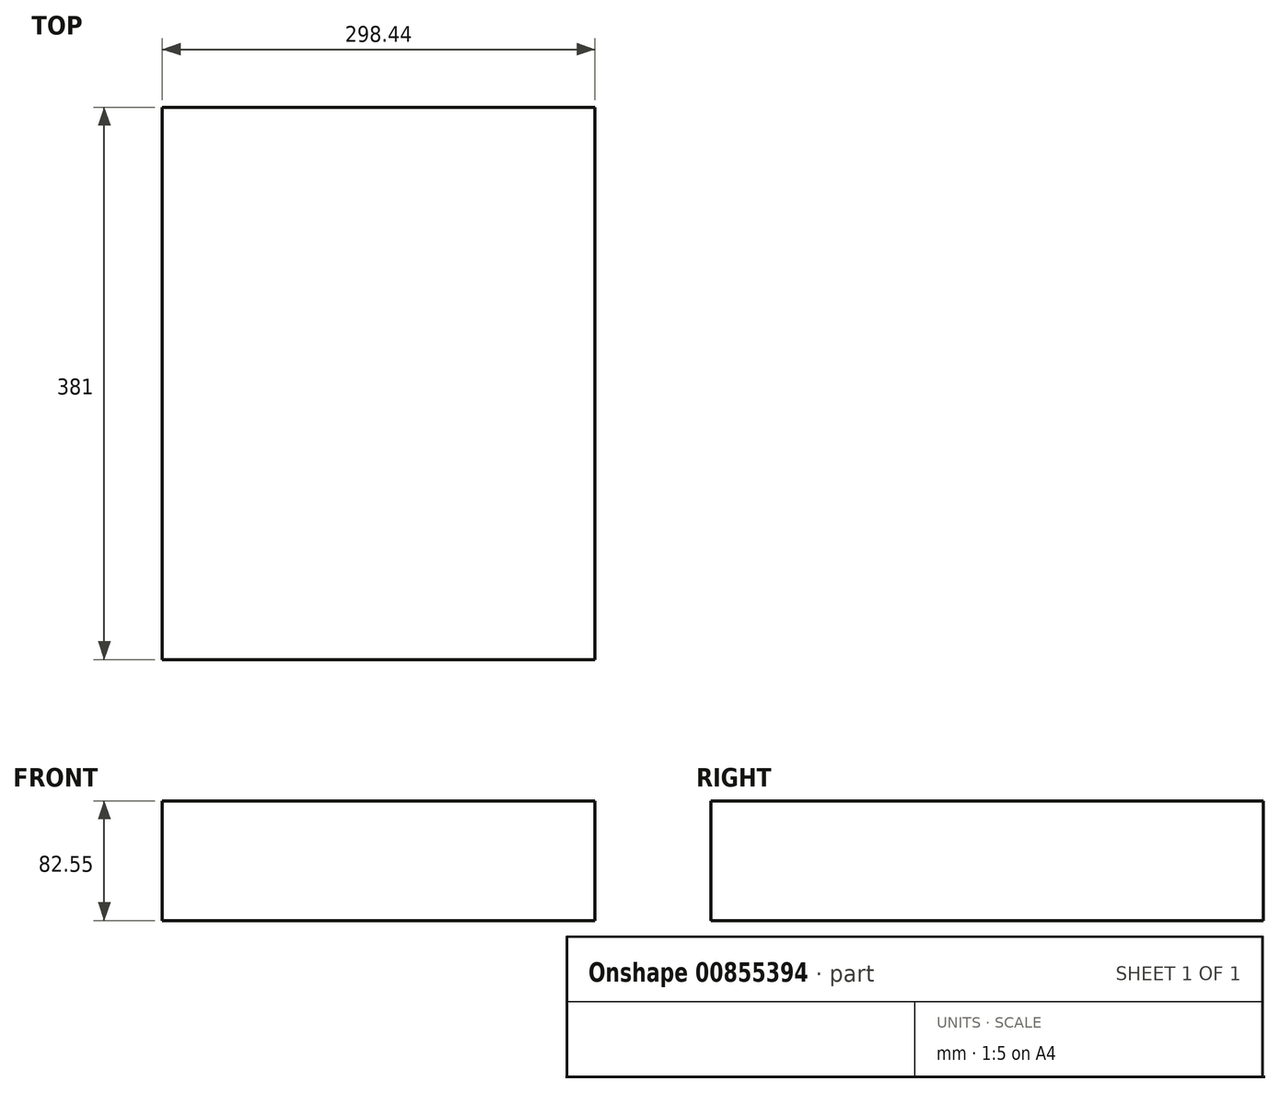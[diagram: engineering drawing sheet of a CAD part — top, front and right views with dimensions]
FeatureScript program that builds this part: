
annotation { "Feature Type Name" : "Feature", "Feature Type Description" : "" }
export const myFeature = defineFeature(function(context is Context, id is Id, definition is map)
    precondition{}
    {
        {
            var Q0;
            Q0=qCreatedBy(makeId("Top.planeOp"),FACE);
            var sketch = newSketch(context, id + "F0", { "sketchPlane" : qUnion([Q0])});
            skLineSegment(sketch, "E0.bottom", {"start": v(-149.23, -190.5) * mm, "end": v(149.22, -190.5) * mm});
            skLineSegment(sketch, "E0.top", {"start": v(-149.22, 190.5) * mm, "end": v(149.23, 190.5) * mm});
            skLineSegment(sketch, "E0.left", {"start": v(-149.23, -190.5) * mm, "end": v(-149.23, 190.5) * mm});
            skLineSegment(sketch, "E0.right", {"start": v(149.22, -190.5) * mm, "end": v(149.23, 190.5) * mm});
            skPoint(sketch, "E0.middle", {"position": v(0, 0) * mm});
            skSolve(sketch);
        }
        {
            var Q0;
            Q0=makeQuery(id+"F0.imprint","IMPRINT",FACE,{"disambiguationData":[TD([[makeQuery(id+"F0.imprint","IMPRINT",EDGE,{"derivedFrom":sQuery(id+"F0.wireOp",EDGE,"E0.bottom")}),1.0]])]});
            extrude(context, id + "F1", {"entities" : qUnion([Q0]), "depth" : 82.55 * mm, "offsetDistance" : 25 * mm});
        }
    });
